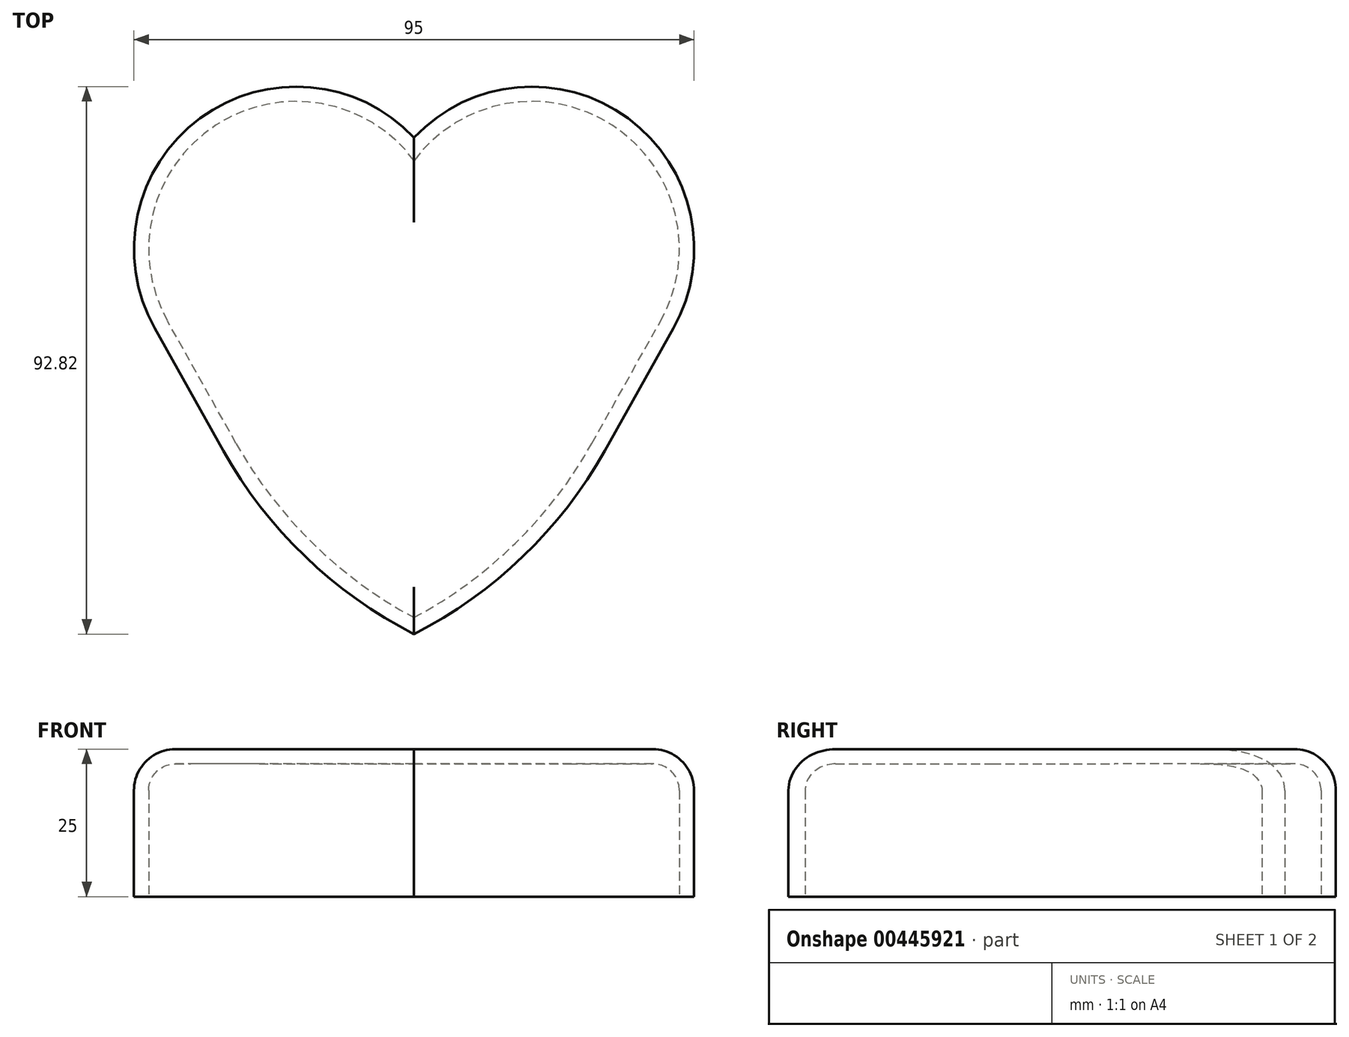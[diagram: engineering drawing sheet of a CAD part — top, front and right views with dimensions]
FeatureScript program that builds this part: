
annotation { "Feature Type Name" : "Feature", "Feature Type Description" : "" }
export const myFeature = defineFeature(function(context is Context, id is Id, definition is map)
    precondition{}
    {
        {
            var Q0;
            Q0=qCreatedBy(makeId("Top.planeOp"),FACE);
            var sketch = newSketch(context, id + "F0", { "sketchPlane" : qUnion([Q0])});
            skLineSegment(sketch, "E0", {"start": v(-32.34, -19.2) * mm, "end": v(-43.98, 1.54) * mm});
            skArc(sketch, "E1", {"start": v(-32.34, -19.2) * mm, "mid": v(-18.47, -37.15) * mm, "end": v(0, -50.32) * mm});
            skLineSegment(sketch, "E2", {"start": v(0, -50.32) * mm, "end": v(0, 33.87) * mm});
            skArc(sketch, "E3", {"start": v(0, 33.87) * mm, "mid": v(-36.29, 37.16) * mm, "end": v(-43.98, 1.54) * mm});
            skSolve(sketch);
        }
        {
            var Q0;
            Q0=makeQuery(id+"F0.imprint","IMPRINT",FACE,{"disambiguationData":[TD([[makeQuery(id+"F0.imprint","IMPRINT",EDGE,{"derivedFrom":sQuery(id+"F0.wireOp",EDGE,"E0")}),-1.0]])]});
            extrude(context, id + "F1", {"entities" : qUnion([Q0]), "depth" : 25 * mm});
        }
        {
            var Q0;
            Q0=makeQuery(id+"F1.opExtrude","SWEPT_BODY",BODY,{"disambiguationData":[OSD([sQuery(id+"F0.wireOp",EDGE,"E0"),sQuery(id+"F0.wireOp",EDGE,"E1"),sQuery(id+"F0.wireOp",EDGE,"E2"),sQuery(id+"F0.wireOp",EDGE,"E3")])]});
            var Q1;
            Q1=qCreatedBy(makeId("Right.planeOp"),FACE);
            mirror(context, id + "F2", {"operationType" : NewBodyOperationType.ADD, "entities" : qUnion([Q0]), "mirrorPlane" : qUnion([Q1])});
        }
        {
            var Q0;
            Q0=makeQuery(id+"F2.opPattern","COPY",EDGE,{"derivedFrom":makeQuery(id+"F1.opExtrude","CAP_EDGE",EDGE,{"disambiguationData":[OSD([sQuery(id+"F0.wireOp",EDGE,"E1")])],"isStart":false}),"instanceName":"1"});
            var Q1;
            Q1=makeQuery(id+"F1.opExtrude","CAP_EDGE",EDGE,{"disambiguationData":[OSD([sQuery(id+"F0.wireOp",EDGE,"E3")])],"isStart":false});
            fillet(context, id + "F3", {"entities" : qUnion([Q0, Q1]), "radius" : 7 * mm, "tangentPropagation" : true, "allowEdgeOverflow" : false});
        }
        {
            var Q0;
            {var subQ0=makeQuery(id+"F1.opExtrude","CAP_FACE",FACE,{"disambiguationData":[OSD([sQuery(id+"F0.wireOp",EDGE,"E0"),sQuery(id+"F0.wireOp",EDGE,"E1"),sQuery(id+"F0.wireOp",EDGE,"E2"),sQuery(id+"F0.wireOp",EDGE,"E3")])],"isStart":true});Q0=makeQuery(id+"F2.boolean.opBoolean","MERGE",FACE,{"derivedFrom":[subQ0,makeQuery(id+"F2.opPattern","COPY",FACE,{"derivedFrom":subQ0,"instanceName":"1"})]});}
            shell(context, id + "F4", {"entities" : qUnion([Q0]), "thickness" : 2.5 * mm});
        }
    });
